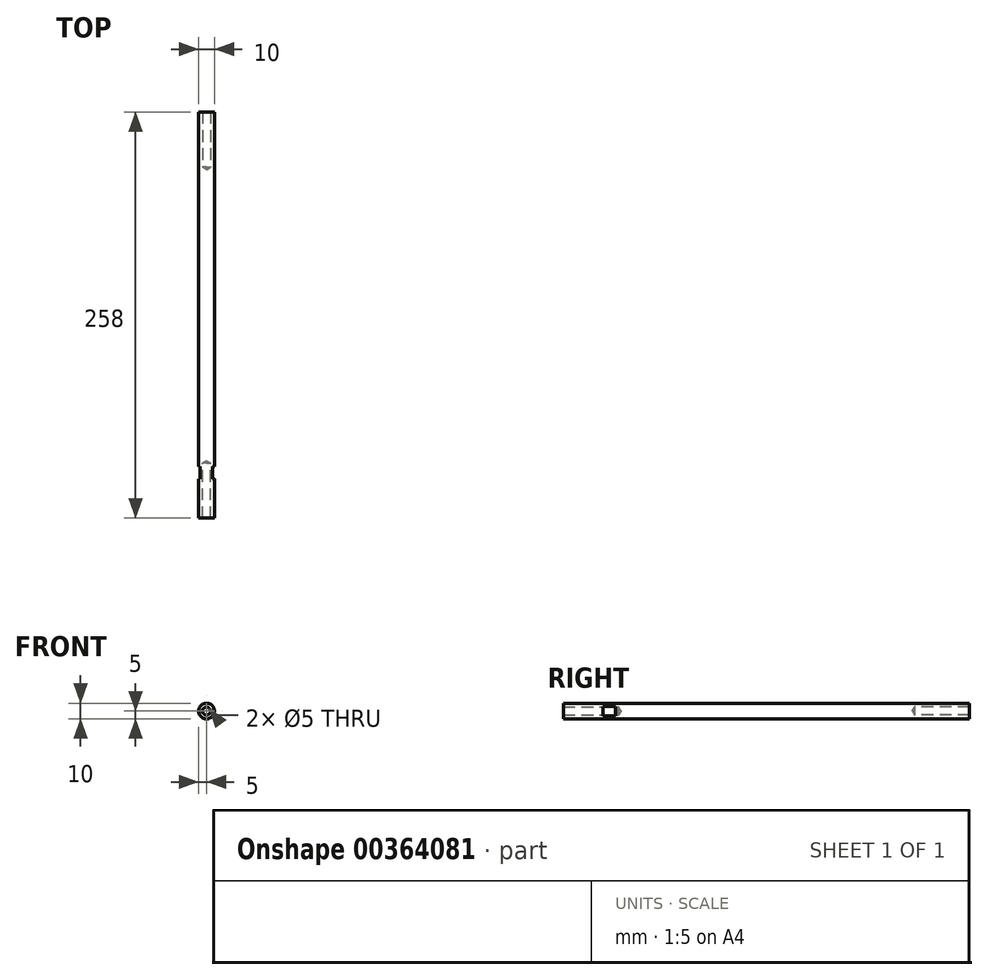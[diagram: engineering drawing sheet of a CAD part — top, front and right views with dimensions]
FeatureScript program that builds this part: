
annotation { "Feature Type Name" : "Feature", "Feature Type Description" : "" }
export const myFeature = defineFeature(function(context is Context, id is Id, definition is map)
    precondition{}
    {
        {
            var Q0;
            Q0=qCreatedBy(makeId("Front.planeOp"),FACE);
            var sketch = newSketch(context, id + "F0", { "sketchPlane" : qUnion([Q0])});
            skCircle(sketch, "E0", {"center": v(0, 0) * mm, "radius": 5 * mm});
            skSolve(sketch);
        }
        {
            var Q0;
            Q0=qSketchRegion(id+"F0",true);
            extrude(context, id + "F1", {"entities" : qUnion([Q0]), "depth" : 258 * mm, "symmetric" : true});
        }
        {
            var Q0;
            Q0=makeQuery(id+"F1.opExtrude","CAP_FACE",FACE,{"disambiguationData":[OSD([sQuery(id+"F0.wireOp",EDGE,"E0")])],"isStart":false});
            var sketch = newSketch(context, id + "F2", { "sketchPlane" : qUnion([Q0])});
            skPoint(sketch, "E1", {"position": v(0, 0) * mm});
            skSolve(sketch);
        }
        {
            var Q0;
            Q0=sQuery(id+"F2.wireOp",VERTEX,"E1");
            var Q1;
            Q1=makeQuery(id+"F1.opExtrude","SWEPT_BODY",BODY,{"disambiguationData":[OSD([sQuery(id+"F0.wireOp",EDGE,"E0")])]});
            hole(context, id + "F3", {"style" : HoleStyle.SIMPLE, "endStyle" : HoleEndStyle.BLIND, "standardTappedOrClearance" : lookupTablePath({ "standard" : "ISO", "engagement" : "75%", "pitch" : "1 mm", "size" : "M6", "type" : "Tapped" }), "standardBlindInLast" : lookupTablePath({ "standard" : "ISO", "engagement" : "75%", "pitch" : "1 mm", "size" : "M6", "type" : "Tapped" }), "holeDiameter" : 5 * mm, "showTappedDepth" : true, "holeDepth" : 35 * mm, "isTappedThrough" : true, "tappedDepth" : 32 * mm, "tapClearance" : 3, "locations" : qUnion([Q0]), "scope" : qUnion([Q1]), "majorDiameter" : 6 * mm, "startStyle" : HoleStartStyle.SKETCH});
        }
        {
            var Q0;
            Q0=makeQuery(id+"F1.opExtrude","CAP_FACE",FACE,{"disambiguationData":[OSD([sQuery(id+"F0.wireOp",EDGE,"E0")])],"isStart":true});
            var sketch = newSketch(context, id + "F4", { "sketchPlane" : qUnion([Q0])});
            skPoint(sketch, "E2", {"position": v(0, 0) * mm});
            skSolve(sketch);
        }
        {
            var Q0;
            Q0=sQuery(id+"F4.wireOp",VERTEX,"E2");
            var Q1;
            Q1=makeQuery(id+"F1.opExtrude","SWEPT_BODY",BODY,{"disambiguationData":[OSD([sQuery(id+"F0.wireOp",EDGE,"E0")])]});
            hole(context, id + "F5", {"style" : HoleStyle.SIMPLE, "endStyle" : HoleEndStyle.BLIND, "standardTappedOrClearance" : lookupTablePath({ "standard" : "ISO", "engagement" : "75%", "pitch" : "1 mm", "size" : "M6", "type" : "Tapped" }), "standardBlindInLast" : lookupTablePath({ "standard" : "ISO", "engagement" : "75%", "pitch" : "1 mm", "size" : "M6", "type" : "Tapped" }), "holeDiameter" : 5 * mm, "showTappedDepth" : true, "holeDepth" : 35 * mm, "isTappedThrough" : true, "tappedDepth" : 30 * mm, "tapClearance" : 5, "locations" : qUnion([Q0]), "scope" : qUnion([Q1]), "majorDiameter" : 6 * mm, "startStyle" : HoleStartStyle.SKETCH});
        }
        {
            var Q0;
            Q0=makeQuery(id+"F1.opExtrude","CAP_FACE",FACE,{"disambiguationData":[OSD([sQuery(id+"F0.wireOp",EDGE,"E0")])],"isStart":false});
            cPlane(context, id + "F6", {"entities" : qUnion([Q0]), "cplaneType" : CPlaneType.OFFSET, "offset" : 25 * mm, "oppositeDirection" : true, "width" : 150 * mm, "height" : 150 * mm});
        }
        {
            var Q0;
            Q0=qCreatedBy(id+"F6.planeOp",FACE);
            var sketch = newSketch(context, id + "F7", { "sketchPlane" : qUnion([Q0])});
            skLineSegment(sketch, "E3", {"start": v(-4, 3) * mm, "end": v(-4, -3) * mm});
            skLineSegment(sketch, "E4", {"start": v(4, 3) * mm, "end": v(4, -3) * mm});
            skLineSegment(sketch, "E5", {"start": v(0, 0) * mm, "end": v(0, 8.9) * mm, "construction": true});
            skCircle(sketch, "E6.0", {"center": v(0, 0) * mm, "radius": 5 * mm});
            skSolve(sketch);
        }
        {
            var Q0;
            {var subQ0=sQuery(id+"F7.wireOp",EDGE,"E3");Q0=makeQuery(id+"F7.imprint","IMPRINT",FACE,{"disambiguationData":[TD([[makeQuery(id+"F7.imprint","IMPRINT",EDGE,{"derivedFrom":subQ0}),-1.0]])]});}
            var Q1;
            {var subQ0=sQuery(id+"F7.wireOp",EDGE,"E4");Q1=makeQuery(id+"F7.imprint","IMPRINT",FACE,{"disambiguationData":[TD([[makeQuery(id+"F7.imprint","IMPRINT",EDGE,{"derivedFrom":subQ0}),1.0]])]});}
            extrude(context, id + "F8", {"entities" : qUnion([Q0, Q1]), "operationType" : NewBodyOperationType.REMOVE, "oppositeDirection" : true, "depth" : 8 * mm});
        }
    });
